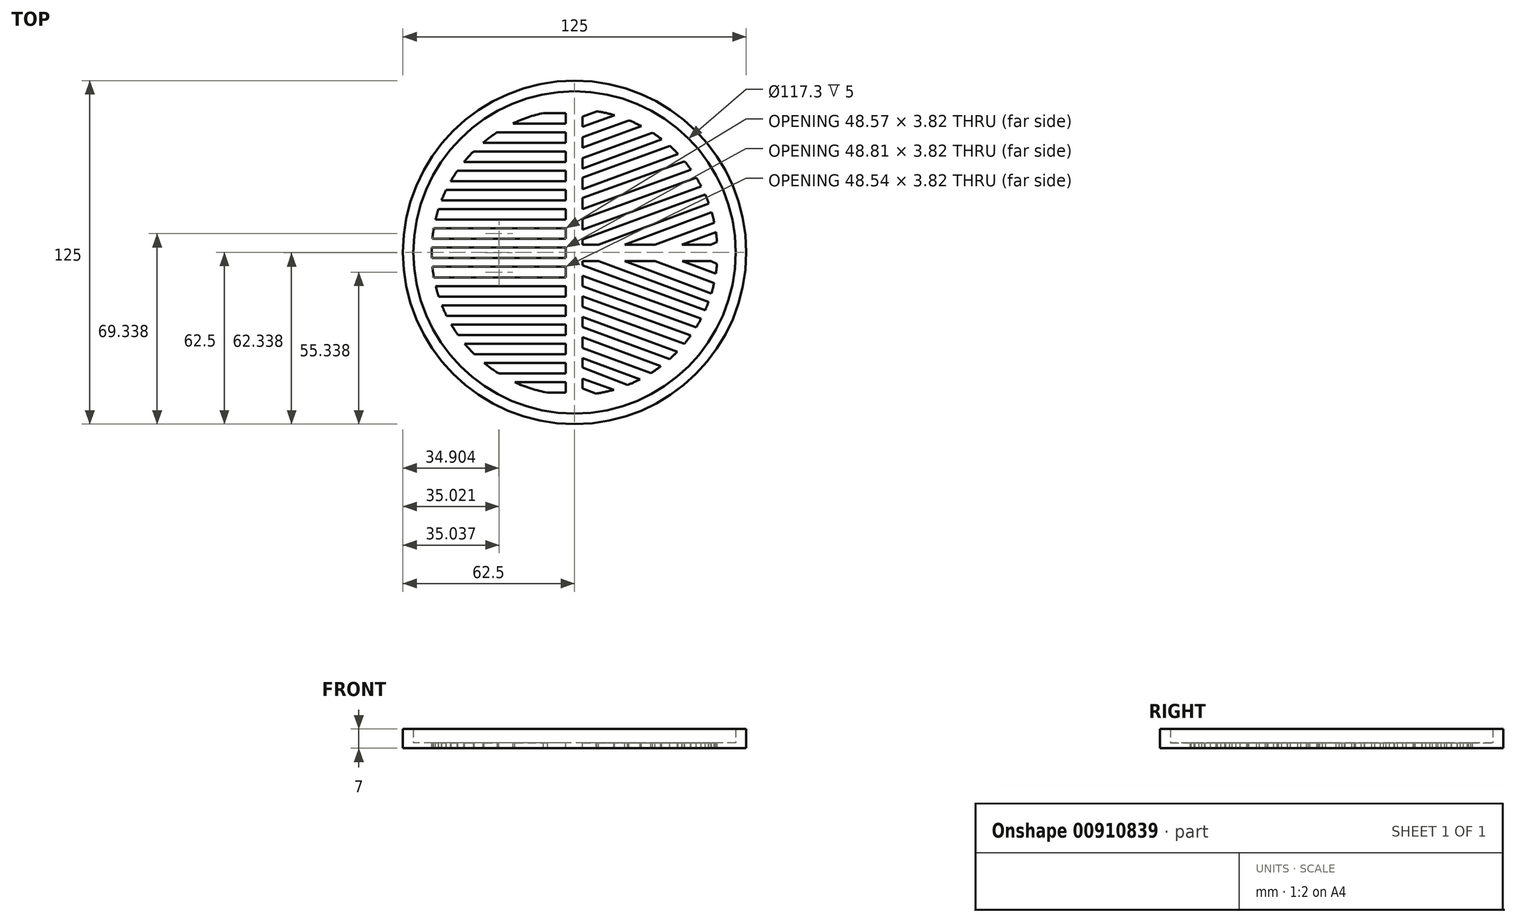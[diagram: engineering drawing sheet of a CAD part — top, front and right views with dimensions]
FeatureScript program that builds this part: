
annotation { "Feature Type Name" : "Feature", "Feature Type Description" : "" }
export const myFeature = defineFeature(function(context is Context, id is Id, definition is map)
    precondition{}
    {
        {
            var Q0;
            Q0=qCreatedBy(makeId("Top.planeOp"),FACE);
            var sketch = newSketch(context, id + "F0", { "sketchPlane" : qUnion([Q0])});
            skArc(sketch, "E0", {"start": v(-11.35, 50.75) * mm, "mid": v(-16.98, 49.15) * mm, "end": v(-22.4, 46.93) * mm});
            skCircle(sketch, "E1", {"center": v(0, 0) * mm, "radius": 62.5 * mm});
            skLineSegment(sketch, "E2", {"start": v(2.9, -49.57) * mm, "end": v(2.9, -45.9) * mm});
            skLineSegment(sketch, "E3", {"start": v(-3.2, -51.07) * mm, "end": v(-3.2, -47.25) * mm});
            skLineSegment(sketch, "E4", {"start": v(2.9, -3.22) * mm, "end": v(8.75, -3.22) * mm});
            skLineSegment(sketch, "E5", {"start": v(2.9, 2.8) * mm, "end": v(8.78, 2.8) * mm});
            skLineSegment(sketch, "E6.trimOffspring", {"start": v(2.9, 2.8) * mm, "end": v(2.9, 4.69) * mm});
            skArc(sketch, "E7.trimOffspring", {"start": v(7.87, -51.4) * mm, "mid": v(11.1, -50.8) * mm, "end": v(14.29, -50) * mm});
            skLineSegment(sketch, "E8", {"start": v(2.9, -49.57) * mm, "end": v(7.87, -51.4) * mm});
            skLineSegment(sketch, "E9", {"start": v(14.29, -50) * mm, "end": v(2.9, -45.9) * mm});
            skLineSegment(sketch, "E10", {"start": v(2.9, -41.94) * mm, "end": v(19.31, -48.28) * mm});
            skLineSegment(sketch, "E11", {"start": v(23.86, -46.2) * mm, "end": v(2.9, -38.46) * mm});
            skLineSegment(sketch, "E12", {"start": v(2.9, -34.8) * mm, "end": v(27.76, -43.97) * mm});
            skLineSegment(sketch, "E13", {"start": v(2.9, -30.82) * mm, "end": v(31.4, -41.45) * mm});
            skLineSegment(sketch, "E14", {"start": v(34.6, -38.83) * mm, "end": v(2.9, -27.2) * mm});
            skLineSegment(sketch, "E15", {"start": v(2.9, -23.52) * mm, "end": v(37.37, -36.16) * mm});
            skLineSegment(sketch, "E16", {"start": v(2.9, -19.83) * mm, "end": v(39.98, -33.25) * mm});
            skLineSegment(sketch, "E17", {"start": v(2.9, -16) * mm, "end": v(42.29, -30.26) * mm});
            skLineSegment(sketch, "E18", {"start": v(2.9, -12.32) * mm, "end": v(44.26, -27.3) * mm});
            skLineSegment(sketch, "E19", {"start": v(2.9, -8.5) * mm, "end": v(46.06, -24.13) * mm});
            skLineSegment(sketch, "E20", {"start": v(2.9, -4.75) * mm, "end": v(47.53, -21.09) * mm});
            skLineSegment(sketch, "E21", {"start": v(8.75, -3.22) * mm, "end": v(48.75, -18.08) * mm});
            skLineSegment(sketch, "E22", {"start": v(18.31, -3.22) * mm, "end": v(49.81, -14.92) * mm});
            skLineSegment(sketch, "E23", {"start": v(29.24, -3.22) * mm, "end": v(50.8, -11.1) * mm});
            skLineSegment(sketch, "E24", {"start": v(39.15, -3.22) * mm, "end": v(51.42, -7.78) * mm});
            skLineSegment(sketch, "E25", {"start": v(49.6, -3.22) * mm, "end": v(51.83, -4.22) * mm});
            skArc(sketch, "E26.trimOffspring", {"start": v(51.86, 3.8) * mm, "mid": v(51.7, 5.61) * mm, "end": v(51.47, 7.42) * mm});
            skArc(sketch, "E27.trimOffspring", {"start": v(51.42, -7.78) * mm, "mid": v(51.65, -6) * mm, "end": v(51.83, -4.22) * mm});
            skArc(sketch, "E28.trimOffspring", {"start": v(49.81, -14.92) * mm, "mid": v(50.34, -13.03) * mm, "end": v(50.8, -11.1) * mm});
            skArc(sketch, "E29.trimOffspring", {"start": v(47.53, -21.09) * mm, "mid": v(48.17, -19.6) * mm, "end": v(48.75, -18.08) * mm});
            skArc(sketch, "E30.trimOffspring", {"start": v(44.26, -27.3) * mm, "mid": v(45.2, -25.73) * mm, "end": v(46.06, -24.13) * mm});
            skArc(sketch, "E31.trimOffspring", {"start": v(39.98, -33.25) * mm, "mid": v(41.16, -31.78) * mm, "end": v(42.29, -30.26) * mm});
            skArc(sketch, "E32.trimOffspring", {"start": v(34.6, -38.83) * mm, "mid": v(36, -37.52) * mm, "end": v(37.37, -36.16) * mm});
            skArc(sketch, "E33.trimOffspring", {"start": v(27.76, -43.97) * mm, "mid": v(29.6, -42.75) * mm, "end": v(31.4, -41.45) * mm});
            skArc(sketch, "E34.trimOffspring", {"start": v(19.31, -48.28) * mm, "mid": v(21.61, -47.3) * mm, "end": v(23.86, -46.2) * mm});
            skLineSegment(sketch, "E35", {"start": v(49.6, 2.8) * mm, "end": v(51.86, 3.8) * mm});
            skLineSegment(sketch, "E36", {"start": v(39.05, 2.8) * mm, "end": v(51.47, 7.42) * mm});
            skLineSegment(sketch, "E37", {"start": v(29.26, 2.8) * mm, "end": v(50.85, 10.87) * mm});
            skLineSegment(sketch, "E38", {"start": v(18.22, 2.8) * mm, "end": v(49.9, 14.64) * mm});
            skLineSegment(sketch, "E39", {"start": v(8.78, 2.8) * mm, "end": v(48.87, 17.76) * mm});
            skLineSegment(sketch, "E40", {"start": v(2.9, 4.69) * mm, "end": v(47.54, 21.07) * mm});
            skLineSegment(sketch, "E41", {"start": v(2.9, 8.25) * mm, "end": v(46.1, 24.06) * mm});
            skLineSegment(sketch, "E42", {"start": v(2.9, 12.17) * mm, "end": v(44.3, 27.23) * mm});
            skLineSegment(sketch, "E43", {"start": v(2.9, 15.76) * mm, "end": v(42.35, 30.17) * mm});
            skLineSegment(sketch, "E44", {"start": v(2.9, 19.79) * mm, "end": v(40.1, 33.11) * mm});
            skLineSegment(sketch, "E45", {"start": v(2.9, 23.03) * mm, "end": v(37.66, 35.86) * mm});
            skLineSegment(sketch, "E46", {"start": v(34.64, 38.78) * mm, "end": v(2.9, 27.16) * mm});
            skLineSegment(sketch, "E47", {"start": v(2.9, 30.53) * mm, "end": v(31.7, 41.22) * mm});
            skLineSegment(sketch, "E48", {"start": v(2.9, 34.33) * mm, "end": v(28.38, 43.57) * mm});
            skLineSegment(sketch, "E49", {"start": v(2.9, 38.13) * mm, "end": v(24.35, 45.95) * mm});
            skLineSegment(sketch, "E50", {"start": v(2.9, 41.93) * mm, "end": v(19.83, 48.07) * mm});
            skLineSegment(sketch, "E51", {"start": v(2.9, 45.73) * mm, "end": v(14.52, 49.93) * mm});
            skLineSegment(sketch, "E52", {"start": v(2.9, 49.4) * mm, "end": v(8.12, 51.36) * mm});
            skArc(sketch, "E53.trimOffspring", {"start": v(14.52, 49.93) * mm, "mid": v(11.34, 50.75) * mm, "end": v(8.12, 51.36) * mm});
            skArc(sketch, "E54.trimOffspring", {"start": v(24.35, 45.95) * mm, "mid": v(22.11, 47.06) * mm, "end": v(19.83, 48.07) * mm});
            skArc(sketch, "E55.trimOffspring", {"start": v(31.7, 41.22) * mm, "mid": v(30.06, 42.43) * mm, "end": v(28.38, 43.57) * mm});
            skArc(sketch, "E56.trimOffspring", {"start": v(37.66, 35.86) * mm, "mid": v(36.18, 37.35) * mm, "end": v(34.64, 38.78) * mm});
            skArc(sketch, "E57.trimOffspring", {"start": v(42.35, 30.17) * mm, "mid": v(41.25, 31.66) * mm, "end": v(40.1, 33.11) * mm});
            skArc(sketch, "E58.trimOffspring", {"start": v(46.1, 24.06) * mm, "mid": v(45.23, 25.66) * mm, "end": v(44.3, 27.23) * mm});
            skArc(sketch, "E59.trimOffspring", {"start": v(48.87, 17.76) * mm, "mid": v(48.24, 19.42) * mm, "end": v(47.54, 21.07) * mm});
            skArc(sketch, "E60.trimOffspring", {"start": v(50.85, 10.87) * mm, "mid": v(50.4, 12.76) * mm, "end": v(49.9, 14.64) * mm});
            skLineSegment(sketch, "E61", {"start": v(-3.2, 50.75) * mm, "end": v(-11.35, 50.75) * mm});
            skLineSegment(sketch, "E62.0.1.0", {"start": v(-3.2, 43.75) * mm, "end": v(-28.11, 43.75) * mm});
            skLineSegment(sketch, "E62.0.2.0", {"start": v(-3.2, 36.75) * mm, "end": v(-36.8, 36.75) * mm});
            skLineSegment(sketch, "E62.0.3.0", {"start": v(-3.2, 29.75) * mm, "end": v(-42.65, 29.75) * mm});
            skLineSegment(sketch, "E62.0.4.0", {"start": v(-3.2, 22.75) * mm, "end": v(-46.76, 22.75) * mm});
            skLineSegment(sketch, "E62.0.5.0", {"start": v(-3.2, 15.75) * mm, "end": v(-49.56, 15.75) * mm});
            skLineSegment(sketch, "E62.0.6.0", {"start": v(-3.2, 8.75) * mm, "end": v(-51.26, 8.75) * mm});
            skLineSegment(sketch, "E62.0.7.0", {"start": v(-3.2, 1.75) * mm, "end": v(-51.97, 1.75) * mm});
            skLineSegment(sketch, "E62.0.8.0", {"start": v(-3.2, -5.25) * mm, "end": v(-51.73, -5.25) * mm});
            skLineSegment(sketch, "E62.0.9.0", {"start": v(-3.2, -12.25) * mm, "end": v(-50.54, -12.25) * mm});
            skLineSegment(sketch, "E62.0.10.0", {"start": v(-3.2, -19.25) * mm, "end": v(-48.3, -19.25) * mm});
            skLineSegment(sketch, "E62.0.11.0", {"start": v(-3.2, -26.25) * mm, "end": v(-44.89, -26.25) * mm});
            skLineSegment(sketch, "E62.0.12.0", {"start": v(-3.2, -33.25) * mm, "end": v(-39.98, -33.25) * mm});
            skLineSegment(sketch, "E62.0.13.0", {"start": v(-3.2, -40.25) * mm, "end": v(-32.92, -40.25) * mm});
            skLineSegment(sketch, "E62.0.14.0", {"start": v(-3.2, -47.25) * mm, "end": v(-21.7, -47.25) * mm});
            skLineSegment(sketch, "E62.direction1", {"start": v(-11.35, 50.75) * mm, "end": v(2.9, 50.75) * mm, "construction": true});
            skLineSegment(sketch, "E62.direction2", {"start": v(-11.35, 50.75) * mm, "end": v(-11.35, 46.93) * mm, "construction": true});
            skPoint(sketch, "E63.orphan", {"position": v(-11.35, 36.75) * mm});
            skPoint(sketch, "E64.orphan", {"position": v(-11.35, 29.75) * mm});
            skPoint(sketch, "E65.orphan", {"position": v(-11.35, 22.75) * mm});
            skPoint(sketch, "E66.orphan", {"position": v(-11.35, 15.75) * mm});
            skPoint(sketch, "E67.orphan", {"position": v(-11.35, 8.75) * mm});
            skPoint(sketch, "E68.orphan", {"position": v(-11.35, 1.75) * mm});
            skPoint(sketch, "E69.orphan", {"position": v(-11.35, -5.25) * mm});
            skPoint(sketch, "E70.orphan", {"position": v(-11.35, -12.25) * mm});
            skPoint(sketch, "E71.orphan", {"position": v(-11.35, -19.25) * mm});
            skPoint(sketch, "E72.orphan", {"position": v(-11.35, -26.25) * mm});
            skPoint(sketch, "E73.orphan", {"position": v(-11.35, -33.25) * mm});
            skPoint(sketch, "E74.orphan", {"position": v(-11.35, -40.25) * mm});
            skPoint(sketch, "E75.orphan", {"position": v(-11.35, -47.25) * mm});
            skLineSegment(sketch, "E76", {"start": v(-3.2, -51.07) * mm, "end": v(-9.79, -51.07) * mm});
            skLineSegment(sketch, "E77.0.1.0", {"start": v(-3.2, -44.07) * mm, "end": v(-27.6, -44.07) * mm});
            skLineSegment(sketch, "E77.0.2.0", {"start": v(-3.2, -37.07) * mm, "end": v(-36.47, -37.07) * mm});
            skLineSegment(sketch, "E77.0.3.0", {"start": v(-3.2, -30.07) * mm, "end": v(-42.42, -30.07) * mm});
            skLineSegment(sketch, "E77.0.4.0", {"start": v(-3.2, -23.07) * mm, "end": v(-46.6, -23.07) * mm});
            skLineSegment(sketch, "E77.0.5.0", {"start": v(-3.2, -16.07) * mm, "end": v(-49.45, -16.07) * mm});
            skLineSegment(sketch, "E77.0.6.0", {"start": v(-3.2, -9.07) * mm, "end": v(-51.2, -9.07) * mm});
            skLineSegment(sketch, "E77.0.7.0", {"start": v(-3.2, -2.07) * mm, "end": v(-51.96, -2.07) * mm});
            skLineSegment(sketch, "E77.0.8.0", {"start": v(-3.2, 4.93) * mm, "end": v(-51.77, 4.93) * mm});
            skLineSegment(sketch, "E77.0.9.0", {"start": v(-3.2, 11.93) * mm, "end": v(-50.61, 11.93) * mm});
            skLineSegment(sketch, "E77.0.10.0", {"start": v(-3.2, 18.93) * mm, "end": v(-48.43, 18.93) * mm});
            skLineSegment(sketch, "E77.0.11.0", {"start": v(-3.2, 25.93) * mm, "end": v(-45.07, 25.93) * mm});
            skLineSegment(sketch, "E77.0.12.0", {"start": v(-3.2, 32.93) * mm, "end": v(-40.24, 32.93) * mm});
            skLineSegment(sketch, "E77.0.13.0", {"start": v(-3.2, 39.93) * mm, "end": v(-33.31, 39.93) * mm});
            skLineSegment(sketch, "E77.0.14.0", {"start": v(-3.2, 46.93) * mm, "end": v(-22.4, 46.93) * mm});
            skLineSegment(sketch, "E77.direction1", {"start": v(-9.79, -51.07) * mm, "end": v(6.97, -51.07) * mm, "construction": true});
            skLineSegment(sketch, "E77.direction2", {"start": v(-9.79, -51.07) * mm, "end": v(-9.79, -47.25) * mm, "construction": true});
            skPoint(sketch, "E78.orphan", {"position": v(-9.79, 46.93) * mm});
            skPoint(sketch, "E79.orphan", {"position": v(-9.79, 39.93) * mm});
            skPoint(sketch, "E80.orphan", {"position": v(-9.79, 32.93) * mm});
            skPoint(sketch, "E81.orphan", {"position": v(-9.79, 25.93) * mm});
            skPoint(sketch, "E82.orphan", {"position": v(-9.79, 18.93) * mm});
            skPoint(sketch, "E83.orphan", {"position": v(-9.79, 11.93) * mm});
            skPoint(sketch, "E84.orphan", {"position": v(-9.79, 4.93) * mm});
            skPoint(sketch, "E85.orphan", {"position": v(-9.79, -2.07) * mm});
            skPoint(sketch, "E86.orphan", {"position": v(-9.79, -9.07) * mm});
            skPoint(sketch, "E87.orphan", {"position": v(-9.79, -16.07) * mm});
            skPoint(sketch, "E88.orphan", {"position": v(-9.79, -23.07) * mm});
            skPoint(sketch, "E89.orphan", {"position": v(-9.79, -30.07) * mm});
            skPoint(sketch, "E90.orphan", {"position": v(-3.2, -37.07) * mm});
            skArc(sketch, "E91.trimOffspring", {"start": v(-28.11, 43.75) * mm, "mid": v(-30.77, 41.92) * mm, "end": v(-33.31, 39.93) * mm});
            skArc(sketch, "E92.trimOffspring", {"start": v(-36.8, 36.75) * mm, "mid": v(-38.57, 34.88) * mm, "end": v(-40.24, 32.93) * mm});
            skArc(sketch, "E93.trimOffspring", {"start": v(-42.65, 29.75) * mm, "mid": v(-43.9, 27.86) * mm, "end": v(-45.07, 25.93) * mm});
            skArc(sketch, "E94.trimOffspring", {"start": v(-46.76, 22.75) * mm, "mid": v(-47.63, 20.85) * mm, "end": v(-48.43, 18.93) * mm});
            skArc(sketch, "E95.trimOffspring", {"start": v(-49.56, 15.75) * mm, "mid": v(-50.12, 13.85) * mm, "end": v(-50.61, 11.93) * mm});
            skArc(sketch, "E96.trimOffspring", {"start": v(-51.26, 8.75) * mm, "mid": v(-51.55, 6.84) * mm, "end": v(-51.77, 4.93) * mm});
            skArc(sketch, "E97.trimOffspring", {"start": v(-51.97, 1.75) * mm, "mid": v(-52, -0.16) * mm, "end": v(-51.96, -2.07) * mm});
            skArc(sketch, "E98.trimOffspring", {"start": v(-51.73, -5.25) * mm, "mid": v(-51.5, -7.17) * mm, "end": v(-51.2, -9.07) * mm});
            skArc(sketch, "E99.trimOffspring", {"start": v(-50.54, -12.25) * mm, "mid": v(-50.03, -14.17) * mm, "end": v(-49.45, -16.07) * mm});
            skArc(sketch, "E100.trimOffspring", {"start": v(-48.3, -19.25) * mm, "mid": v(-47.5, -21.18) * mm, "end": v(-46.6, -23.07) * mm});
            skArc(sketch, "E101.trimOffspring", {"start": v(-44.89, -26.25) * mm, "mid": v(-43.7, -28.19) * mm, "end": v(-42.42, -30.07) * mm});
            skArc(sketch, "E102.trimOffspring", {"start": v(-39.98, -33.25) * mm, "mid": v(-38.27, -35.2) * mm, "end": v(-36.47, -37.07) * mm});
            skArc(sketch, "E103.trimOffspring", {"start": v(-32.92, -40.25) * mm, "mid": v(-30.32, -42.25) * mm, "end": v(-27.6, -44.07) * mm});
            skArc(sketch, "E104.trimOffspring", {"start": v(-21.7, -47.25) * mm, "mid": v(-15.86, -49.52) * mm, "end": v(-9.79, -51.07) * mm});
            skPoint(sketch, "E105.orphan", {"position": v(-11.35, 43.75) * mm});
            skPoint(sketch, "E106.orphan", {"position": v(-9.79, -44.07) * mm});
            skCircle(sketch, "E107", {"center": v(0, 0) * mm, "radius": 58.65 * mm});
            skLineSegment(sketch, "E108.trimOffspring", {"start": v(-3.2, 46.93) * mm, "end": v(-3.2, 50.75) * mm});
            skLineSegment(sketch, "E109.trimOffspring", {"start": v(-3.2, 39.93) * mm, "end": v(-3.2, 43.75) * mm});
            skLineSegment(sketch, "E110.trimOffspring", {"start": v(-3.2, 32.93) * mm, "end": v(-3.2, 36.75) * mm});
            skLineSegment(sketch, "E111.trimOffspring", {"start": v(-3.2, 25.93) * mm, "end": v(-3.2, 29.75) * mm});
            skLineSegment(sketch, "E112.trimOffspring", {"start": v(-3.2, 18.93) * mm, "end": v(-3.2, 22.75) * mm});
            skLineSegment(sketch, "E113.trimOffspring", {"start": v(-3.2, 11.93) * mm, "end": v(-3.2, 15.75) * mm});
            skLineSegment(sketch, "E114.trimOffspring", {"start": v(-3.2, 4.93) * mm, "end": v(-3.2, 8.75) * mm});
            skLineSegment(sketch, "E115.trimOffspring", {"start": v(-3.2, -2.07) * mm, "end": v(-3.2, 1.75) * mm});
            skLineSegment(sketch, "E116.trimOffspring", {"start": v(-3.2, -9.07) * mm, "end": v(-3.2, -5.25) * mm});
            skLineSegment(sketch, "E117.trimOffspring", {"start": v(-3.2, -16.07) * mm, "end": v(-3.2, -12.25) * mm});
            skLineSegment(sketch, "E118.trimOffspring", {"start": v(-3.2, -23.07) * mm, "end": v(-3.2, -19.25) * mm});
            skLineSegment(sketch, "E119.trimOffspring", {"start": v(-3.2, -30.07) * mm, "end": v(-3.2, -26.25) * mm});
            skPoint(sketch, "E120.orphan", {"position": v(-9.79, -37.07) * mm});
            skLineSegment(sketch, "E121.trimOffspring", {"start": v(-3.2, -37.07) * mm, "end": v(-3.2, -33.25) * mm});
            skLineSegment(sketch, "E122.trimOffspring", {"start": v(-3.2, -44.07) * mm, "end": v(-3.2, -40.25) * mm});
            skLineSegment(sketch, "E123.trimOffspring", {"start": v(2.9, -41.94) * mm, "end": v(2.9, -38.46) * mm});
            skLineSegment(sketch, "E124.trimOffspring", {"start": v(2.9, -34.8) * mm, "end": v(2.9, -30.82) * mm});
            skLineSegment(sketch, "E125.trimOffspring", {"start": v(2.9, -27.2) * mm, "end": v(2.9, -23.52) * mm});
            skLineSegment(sketch, "E126.trimOffspring", {"start": v(2.9, -19.83) * mm, "end": v(2.9, -16) * mm});
            skLineSegment(sketch, "E127.trimOffspring", {"start": v(2.9, -12.32) * mm, "end": v(2.9, -8.5) * mm});
            skLineSegment(sketch, "E128.trimOffspring", {"start": v(2.9, -4.75) * mm, "end": v(2.9, -3.22) * mm});
            skLineSegment(sketch, "E129.trimOffspring", {"start": v(18.31, -3.22) * mm, "end": v(29.24, -3.22) * mm});
            skLineSegment(sketch, "E130.trimOffspring", {"start": v(39.15, -3.22) * mm, "end": v(49.6, -3.22) * mm});
            skLineSegment(sketch, "E131.trimOffspring", {"start": v(39.05, 2.8) * mm, "end": v(49.6, 2.8) * mm});
            skLineSegment(sketch, "E132.trimOffspring", {"start": v(18.22, 2.8) * mm, "end": v(29.26, 2.8) * mm});
            skLineSegment(sketch, "E133.trimOffspring", {"start": v(2.9, 8.25) * mm, "end": v(2.9, 12.17) * mm});
            skLineSegment(sketch, "E134.trimOffspring", {"start": v(2.9, 15.76) * mm, "end": v(2.9, 19.79) * mm});
            skLineSegment(sketch, "E135.trimOffspring", {"start": v(2.9, 23.03) * mm, "end": v(2.9, 27.16) * mm});
            skLineSegment(sketch, "E136.trimOffspring", {"start": v(2.9, 30.53) * mm, "end": v(2.9, 34.33) * mm});
            skLineSegment(sketch, "E137.trimOffspring", {"start": v(2.9, 38.13) * mm, "end": v(2.9, 41.93) * mm});
            skLineSegment(sketch, "E138.trimOffspring", {"start": v(2.9, 45.73) * mm, "end": v(2.9, 49.4) * mm});
            skSolve(sketch);
        }
        {
            var Q0;
            Q0=makeQuery(id+"F0.imprint","IMPRINT",FACE,{"disambiguationData":[TD([[makeQuery(id+"F0.imprint","IMPRINT",EDGE,{"derivedFrom":sQuery(id+"F0.wireOp",EDGE,"E1")}),1.0]])]});
            var Q1;
            Q1=makeQuery(id+"F0.imprint","IMPRINT",FACE,{"disambiguationData":[TD([[makeQuery(id+"F0.imprint","IMPRINT",EDGE,{"derivedFrom":sQuery(id+"F0.wireOp",EDGE,"E0")}),-1.0]])]});
            extrude(context, id + "F1", {"entities" : qUnion([Q0, Q1]), "oppositeDirection" : true, "depth" : 2 * mm, "offsetDistance" : 25 * mm});
        }
        {
            var Q0;
            Q0=makeQuery(id+"F0.imprint","IMPRINT",FACE,{"disambiguationData":[TD([[makeQuery(id+"F0.imprint","IMPRINT",EDGE,{"derivedFrom":sQuery(id+"F0.wireOp",EDGE,"E1")}),1.0]])]});
            extrude(context, id + "F2", {"entities" : qUnion([Q0]), "operationType" : NewBodyOperationType.ADD, "depth" : 5 * mm, "offsetDistance" : 25 * mm});
        }
    });
